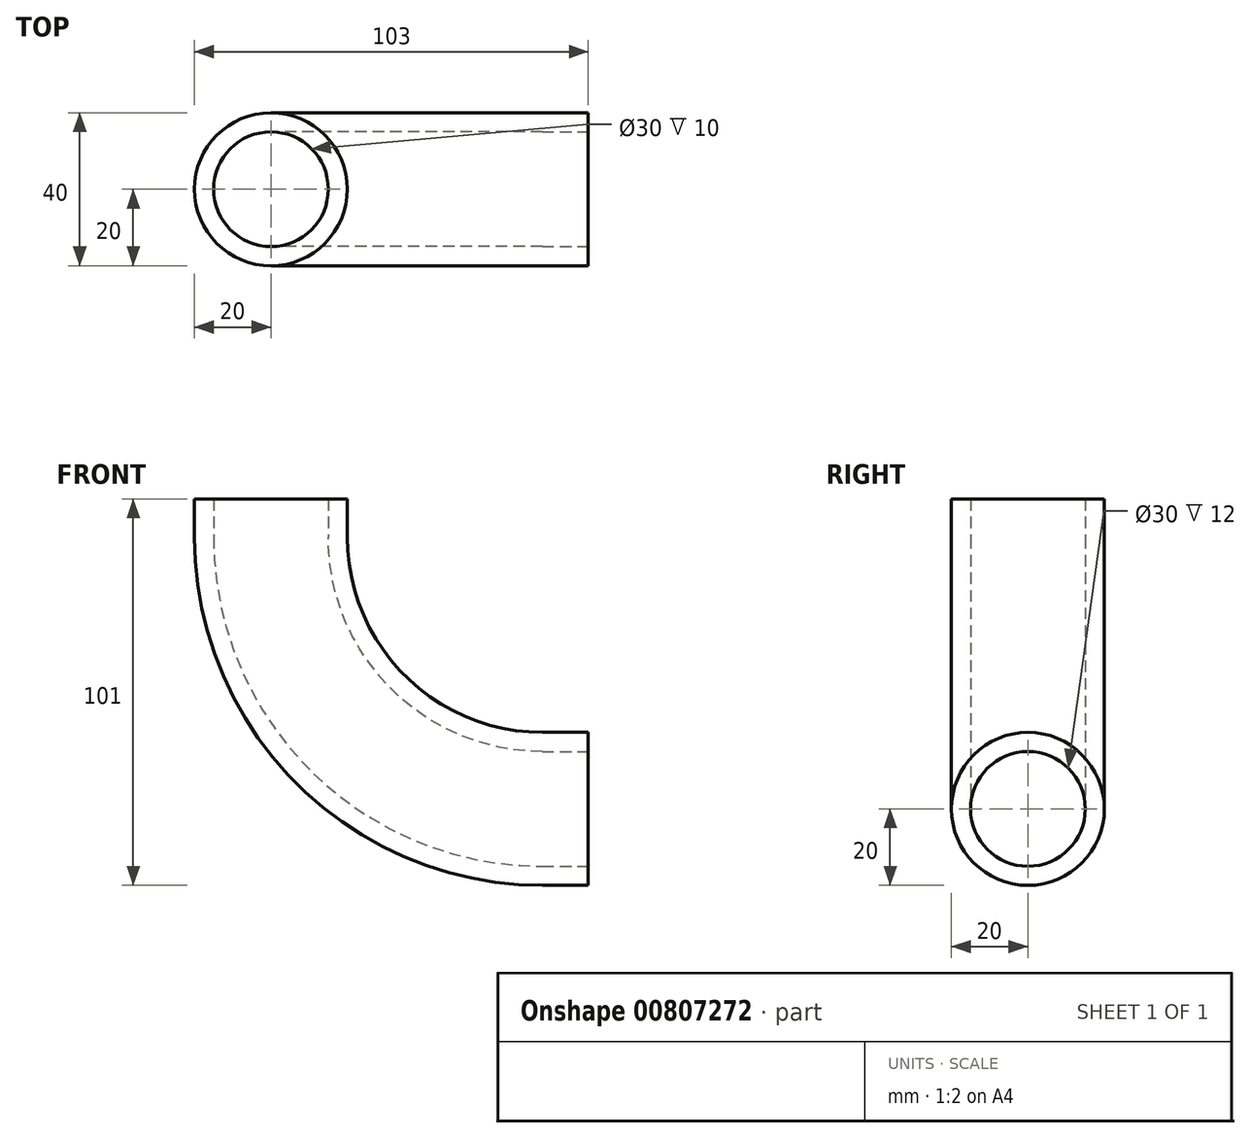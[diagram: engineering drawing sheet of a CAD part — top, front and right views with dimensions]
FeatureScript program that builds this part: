
annotation { "Feature Type Name" : "Feature", "Feature Type Description" : "" }
export const myFeature = defineFeature(function(context is Context, id is Id, definition is map)
    precondition{}
    {
        {
            var Q0;
            Q0=qCreatedBy(makeId("Top.planeOp"),FACE);
            var sketch = newSketch(context, id + "F0", { "sketchPlane" : qUnion([Q0])});
            skCircle(sketch, "E0", {"center": v(0, 0) * mm, "radius": 20 * mm});
            skSolve(sketch);
        }
        {
            var Q0;
            Q0=qCreatedBy(makeId("Front.planeOp"),FACE);
            var sketch = newSketch(context, id + "F1", { "sketchPlane" : qUnion([Q0])});
            skLineSegment(sketch, "E1", {"start": v(0, 0) * mm, "end": v(0, -10) * mm});
            skArc(sketch, "E2", {"start": v(0, -10) * mm, "mid": v(20.8, -60.2) * mm, "end": v(71, -81) * mm});
            skLineSegment(sketch, "E3", {"start": v(71, -81) * mm, "end": v(83, -81) * mm});
            skSolve(sketch);
        }
        {
            var Q0;
            Q0=qCreatedBy(makeId("Right.planeOp"),FACE);
            cPlane(context, id + "F2", {"entities" : qUnion([Q0]), "cplaneType" : CPlaneType.OFFSET, "offset" : (71 + 12) * mm, "width" : 150 * mm, "height" : 150 * mm});
        }
        {
            var Q0;
            Q0=qCreatedBy(id+"F2.planeOp",FACE);
            var sketch = newSketch(context, id + "F3", { "sketchPlane" : qUnion([Q0])});
            skPoint(sketch, "E4.0", {"position": v(0, -81) * mm});
            skCircle(sketch, "E5", {"center": v(0, -81) * mm, "radius": 20 * mm});
            skSolve(sketch);
        }
        {
            var Q0;
            Q0=makeQuery(id+"F0.imprint","IMPRINT",FACE,{"disambiguationData":[TD([[makeQuery(id+"F0.imprint","IMPRINT",EDGE,{"derivedFrom":sQuery(id+"F0.wireOp",EDGE,"E0")}),1.0]])]});
            var Q1;
            Q1=makeQuery(id+"F3.imprint","IMPRINT",FACE,{"disambiguationData":[TD([[makeQuery(id+"F3.imprint","IMPRINT",EDGE,{"derivedFrom":sQuery(id+"F3.wireOp",EDGE,"E5")}),1.0]])]});
            var Q2;
            Q2=sQuery(id+"F1.wireOp",EDGE,"E1");
            var Q3;
            Q3=sQuery(id+"F1.wireOp",EDGE,"E2");
            var Q4;
            Q4=sQuery(id+"F1.wireOp",EDGE,"E3");
            sweep(context, id + "F4", {"profiles" : qUnion([Q0, Q1]), "path" : qUnion([Q2, Q3, Q4])});
        }
        {
            var Q0;
            Q0=makeQuery(id+"F4.opSweep","CAP_FACE",FACE,{"disambiguationData":[OSD([sQuery(id+"F0.wireOp",EDGE,"E0"),sQuery(id+"F1.wireOp",VERTEX,"E1.start")])],"isStart":true});
            var Q1;
            Q1=makeQuery(id+"F4.opSweep","CAP_FACE",FACE,{"disambiguationData":[OSD([sQuery(id+"F0.wireOp",EDGE,"E0"),sQuery(id+"F1.wireOp",VERTEX,"E3.end")])],"isStart":false});
            shell(context, id + "F5", {"entities" : qUnion([Q0, Q1]), "thickness" : 5 * mm});
        }
    });
